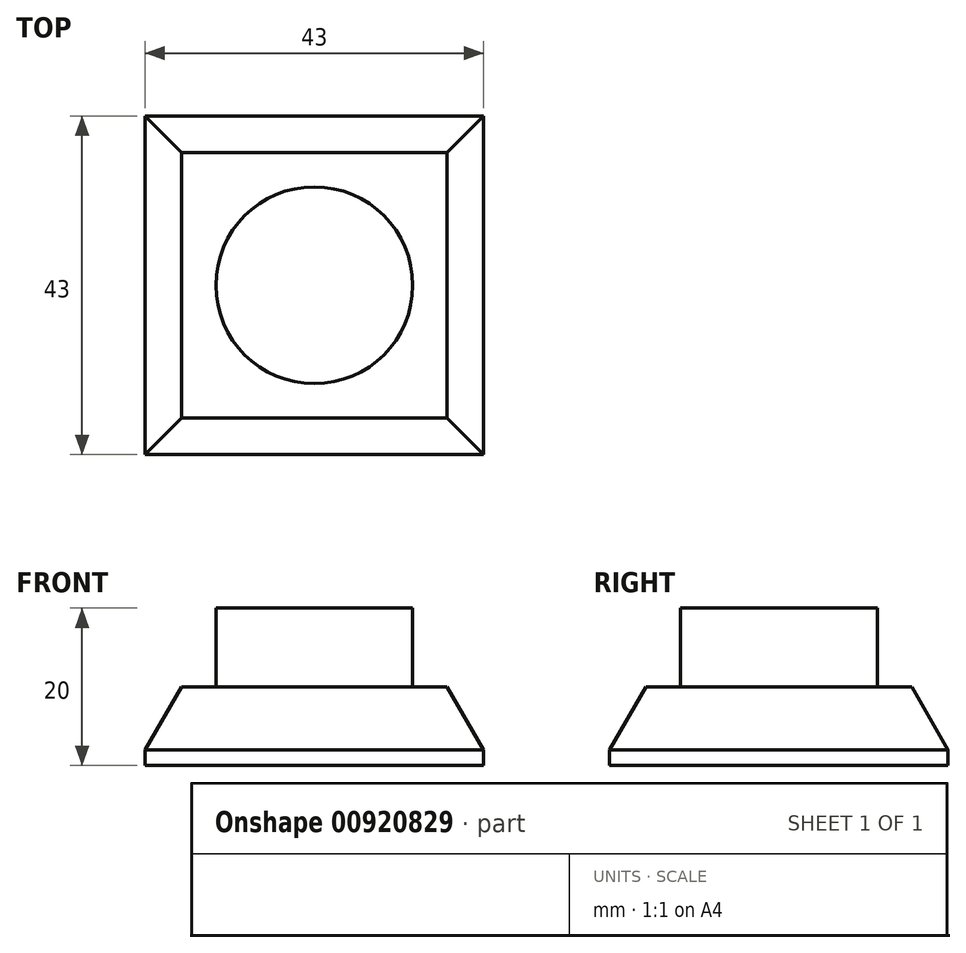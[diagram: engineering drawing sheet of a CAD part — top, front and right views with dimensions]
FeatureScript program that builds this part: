
annotation { "Feature Type Name" : "Feature", "Feature Type Description" : "" }
export const myFeature = defineFeature(function(context is Context, id is Id, definition is map)
    precondition{}
    {
        {
            var Q0;
            Q0=qCreatedBy(makeId("Top.planeOp"),FACE);
            var sketch = newSketch(context, id + "F0", { "sketchPlane" : qUnion([Q0])});
            skLineSegment(sketch, "E0.bottom", {"start": v(21.5, 21.5) * mm, "end": v(-21.5, 21.5) * mm});
            skLineSegment(sketch, "E0.top", {"start": v(21.5, -21.5) * mm, "end": v(-21.5, -21.5) * mm});
            skLineSegment(sketch, "E0.left", {"start": v(21.5, 21.5) * mm, "end": v(21.5, -21.5) * mm});
            skLineSegment(sketch, "E0.right", {"start": v(-21.5, 21.5) * mm, "end": v(-21.5, -21.5) * mm});
            skPoint(sketch, "E0.middle", {"position": v(0, 0) * mm});
            skSolve(sketch);
        }
        {
            var Q0;
            Q0=makeQuery(id+"F0.imprint","IMPRINT",FACE,{"disambiguationData":[TD([[makeQuery(id+"F0.imprint","IMPRINT",EDGE,{"derivedFrom":sQuery(id+"F0.wireOp",EDGE,"E0.bottom")}),1.0]])]});
            extrude(context, id + "F1", {"entities" : qUnion([Q0]), "depth" : 2 * mm, "offsetDistance" : 25 * mm});
        }
        {
            var Q0;
            Q0=makeQuery(id+"F1.opExtrude","CAP_FACE",FACE,{"disambiguationData":[OSD([sQuery(id+"F0.wireOp",EDGE,"E0.bottom"),sQuery(id+"F0.wireOp",EDGE,"E0.top"),sQuery(id+"F0.wireOp",EDGE,"E0.left"),sQuery(id+"F0.wireOp",EDGE,"E0.right")])],"isStart":false});
            extrude(context, id + "F2", {"entities" : qUnion([Q0]), "operationType" : NewBodyOperationType.ADD, "flatOperationType" : FlatOperationType.REMOVE, "depth" : 8 * mm, "offsetDistance" : 25 * mm, "hasDraft" : true, "draftAngle" : 30 * degree, "draftPullDirection" : true, "domain" : OperationDomain.MODEL});
        }
        {
            var Q0;
            Q0=makeQuery(id+"F2.opExtrude","CAP_FACE",FACE,{"disambiguationData":[OSD([sQuery(id+"F0.wireOp",EDGE,"E0.bottom"),sQuery(id+"F0.wireOp",EDGE,"E0.top"),sQuery(id+"F0.wireOp",EDGE,"E0.left"),sQuery(id+"F0.wireOp",EDGE,"E0.right")])],"isStart":false});
            var sketch = newSketch(context, id + "F3", { "sketchPlane" : qUnion([Q0])});
            skCircle(sketch, "E1", {"center": v(0, 0) * mm, "radius": 12.5 * mm});
            skSolve(sketch);
        }
        {
            var Q0;
            Q0=makeQuery(id+"F3.imprint","IMPRINT",FACE,{"disambiguationData":[TD([[makeQuery(id+"F3.imprint","IMPRINT",EDGE,{"derivedFrom":sQuery(id+"F3.wireOp",EDGE,"E1")}),1.0]])]});
            extrude(context, id + "F4", {"entities" : qUnion([Q0]), "operationType" : NewBodyOperationType.ADD, "flatOperationType" : FlatOperationType.REMOVE, "depth" : 10 * mm, "offsetDistance" : 25 * mm, "domain" : OperationDomain.MODEL});
        }
    });
